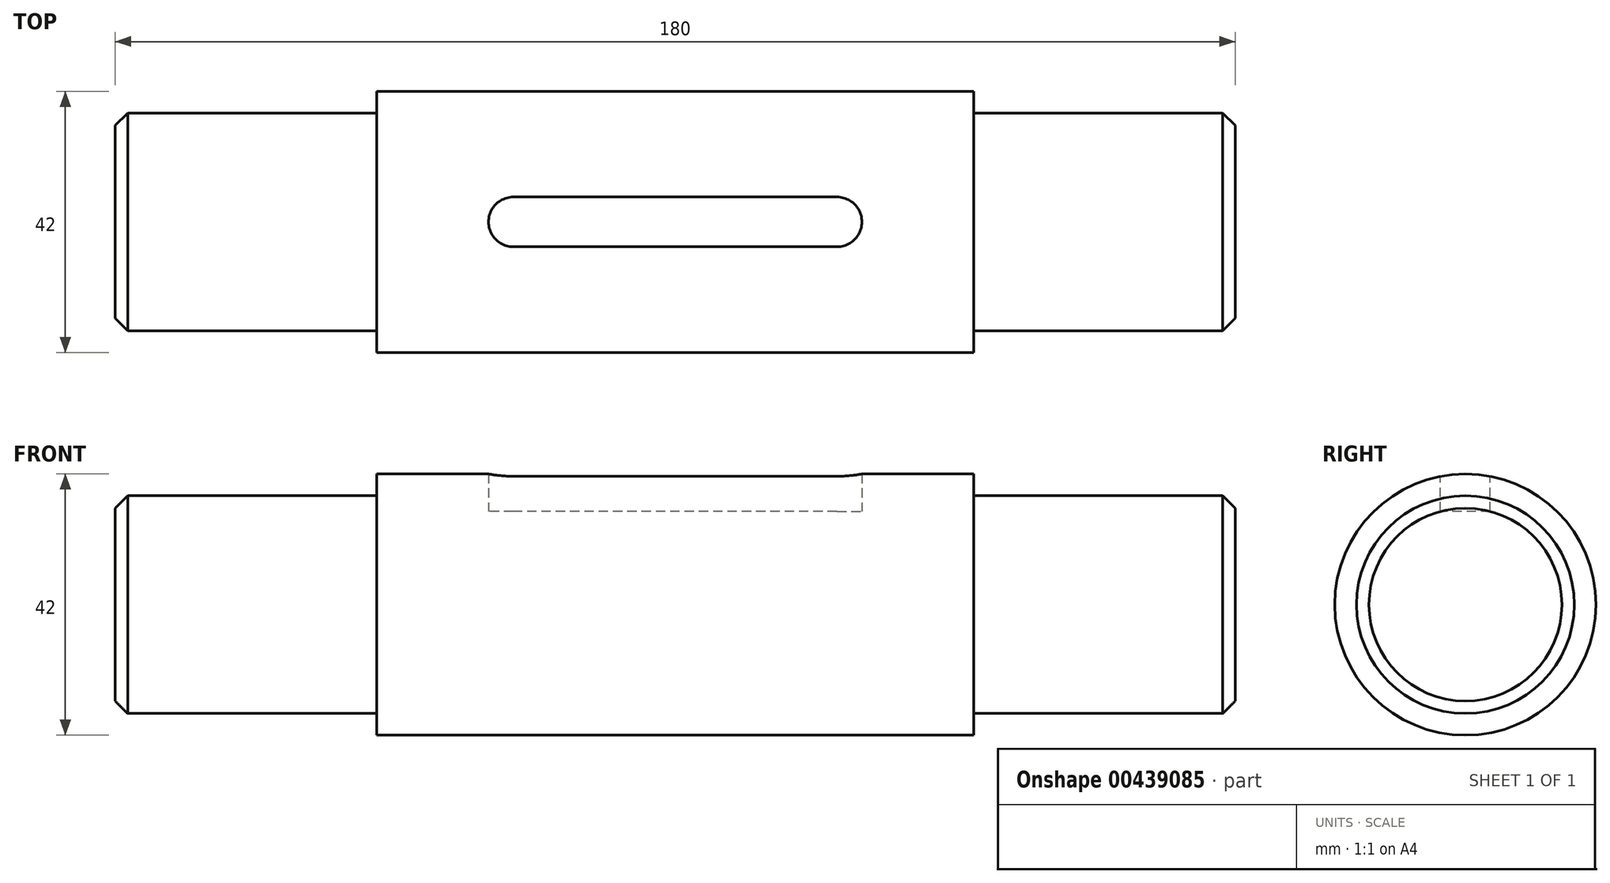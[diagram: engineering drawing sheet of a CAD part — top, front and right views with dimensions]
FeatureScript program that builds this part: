
annotation { "Feature Type Name" : "Feature", "Feature Type Description" : "" }
export const myFeature = defineFeature(function(context is Context, id is Id, definition is map)
    precondition{}
    {
        {
            var Q0;
            Q0=qCreatedBy(makeId("Right.planeOp"),FACE);
            var sketch = newSketch(context, id + "F0", { "sketchPlane" : qUnion([Q0])});
            skCircle(sketch, "E0", {"center": v(0, 0) * mm, "radius": 21 * mm});
            skSolve(sketch);
        }
        {
            var Q0;
            Q0 = qSketchRegion(id + "F0", true);
            extrude(context, id + "F1", {"entities" : qUnion([Q0]), "depth" : 48 * mm});
        }
        {
            var Q0;
            Q0=makeQuery(id+"F1.opExtrude","CAP_FACE",FACE,{"disambiguationData":[OSD([sQuery(id+"F0.wireOp",EDGE,"E0")])],"isStart":false});
            var sketch = newSketch(context, id + "F2", { "sketchPlane" : qUnion([Q0])});
            skCircle(sketch, "E1", {"center": v(0, 0) * mm, "radius": 17.5 * mm});
            skSolve(sketch);
        }
        {
            var Q0;
            Q0 = qSketchRegion(id + "F2", true);
            extrude(context, id + "F3", {"entities" : qUnion([Q0]), "operationType" : NewBodyOperationType.ADD, "depth" : 42 * mm});
        }
        {
            var Q0;
            Q0=makeQuery(id+"F3.opExtrude","CAP_EDGE",EDGE,{"disambiguationData":[OSD([sQuery(id+"F2.wireOp",EDGE,"E1")])],"isStart":false});
            chamfer(context, id + "F4", {"entities" : qUnion([Q0]), "width" : 2 * mm, "tangentPropagation" : true});
        }
        {
            var Q0;
            Q0=makeQuery(id+"F1.opExtrude","CAP_FACE",FACE,{"disambiguationData":[OSD([sQuery(id+"F0.wireOp",EDGE,"E0")])],"isStart":true});
            var sketch = newSketch(context, id + "F5", { "sketchPlane" : qUnion([Q0])});
            skLineSegment(sketch, "E2.bottom", {"start": v(-4, 15) * mm, "end": v(4, 15) * mm});
            skLineSegment(sketch, "E2.top", {"start": v(-4, 27) * mm, "end": v(4, 27) * mm});
            skLineSegment(sketch, "E2.left", {"start": v(-4, 15) * mm, "end": v(-4, 27) * mm});
            skLineSegment(sketch, "E2.right", {"start": v(4, 15) * mm, "end": v(4, 27) * mm});
            skSolve(sketch);
        }
        {
            var Q0;
            Q0 = qSketchRegion(id + "F5", true);
            extrude(context, id + "F6", {"entities" : qUnion([Q0]), "operationType" : NewBodyOperationType.REMOVE, "oppositeDirection" : true, "depth" : 30 * mm});
        }
        {
            var Q0;
            Q0=makeQuery(id+"F6.boolean.opBoolean","COPY",EDGE,{"derivedFrom":makeQuery(id+"F6.opExtrude","CAP_EDGE",EDGE,{"disambiguationData":[OSD([sQuery(id+"F5.wireOp",EDGE,"E2.left")])],"isStart":false})});
            var Q1;
            Q1=makeQuery(id+"F6.boolean.opBoolean","COPY",EDGE,{"derivedFrom":makeQuery(id+"F6.opExtrude","CAP_EDGE",EDGE,{"disambiguationData":[OSD([sQuery(id+"F5.wireOp",EDGE,"E2.right")])],"isStart":false})});
            fillet(context, id + "F7", {"entities" : qUnion([Q0, Q1]), "radius" : 4 * mm, "tangentPropagation" : true, "allowEdgeOverflow" : false});
        }
        {
            var Q0;
            Q0=makeQuery(id+"F1.opExtrude","SWEPT_BODY",BODY,{"disambiguationData":[OSD([sQuery(id+"F0.wireOp",EDGE,"E0")])]});
            var Q1;
            Q1=makeQuery(id+"F1.opExtrude","CAP_FACE",FACE,{"disambiguationData":[OSD([sQuery(id+"F0.wireOp",EDGE,"E0")])],"isStart":true});
            mirror(context, id + "F8", {"operationType" : NewBodyOperationType.ADD, "entities" : qUnion([Q0]), "mirrorPlane" : qUnion([Q1])});
        }
    });
